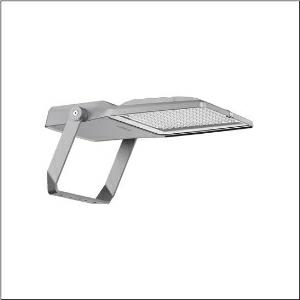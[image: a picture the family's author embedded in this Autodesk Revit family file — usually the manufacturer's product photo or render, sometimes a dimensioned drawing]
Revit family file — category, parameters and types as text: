
# Revit family: floodlight_fl_21_iq_midi___rs12_5xa7782f3b1a_f18b
name_source: partatom
category: Lighting Fixtures
units: mm (PartAtom-declared; Revit-internal decimal feet)

## family parameters
Cut with Voids When Loaded = No
Host = Face
Light Source = No
Part Type = Normal
Room Calculation Point = No
Round Connector Dimension = Use Diameter
Shared = No

## types (1)
- --- (1 x LED, 30610 lm, 270.2 W, 3000K)
    Apparent Load = 270 VA
    CIE Flux Codes = 79 92 99 100 100
    Color Rendering = 80
    Color Temperature = 3000K
    Default Elevation = 1800 mm
    Description = Floodlight FL 21 iQ midi, floodlight, primary light control with lens, of PMMA, primary optical cover: protective disc, of toughened safety glass, transparent, light distribution: RS12, light emission: direct distribution, installation type: surface-mounted, LED, High Power LED, rated luminous flux: 30.610lm, luminous efficacy: 113lm/W, light colour: 830, colour temperature: 3000K, control gear: iQ Street-Remote/DALI, control: optimised constant luminous flux control (CLO 2.0), Desk-Remote (wireless, voltage-free reading and setting of iQ features in the workshop via application-optimized NFC function/RFID function), Smart-Wire, Night-Set, Temp-Guard, Street-Remote, Auto-Match, with terminal, 6-pole, mains connection: 220..240V, AC, 50/60Hz, start of lifetime: 270W, end of service life: 287W, reduction: 117W, luminaire housing, of diecast aluminium, powder-coated, Siteco® metallic grey (DB 702S), corrosivity category C5 mid according to DIN EN ISO 12944, suitable for swimming pools, chlorine-resistant, sealing non-destructively replaceable, mounting bracket, of steel, galvanised, powder-coated, Siteco® metallic grey (DB 702S), protection rating (complete): IP66, insulation class (complete): insulation class II (safety insulation), certification: CE, ENEC, VDE, protection symbol: D, impact resistance: IK08, permissible operating ambient temperature: -40..+40°C, permissible operating ambient temperature for outdoor applications: -40..+50°C, standard: DIN EN 12944, LABS conformity tested according to VDMA 24364:2018-05, packaging unit: 1 piece

Light Distribution: RS12
    Height = 76 mm
    Lamp = 1 x LED
    Lamp Light Flux = 30610 lm
    Lamp Power = 270.2 W
    Lamp count = 1
    Length = 657 mm
    Luminous efficacy = 113 lm/W
    Manufacturer = Siteco
    ModVariant = No
    Model = 5XA7782F3B1A
    Number of Poles = 1
    OnlyDefault = Yes
    Power Factor = 1
    Product Name = Floodlight FL 21 iQ midi | RS12
    Product group = floodlight | pylon annexe
    ProductGroupID = 6200
    Protection Class = Protection class II
    Protection Degree = IP 66
    RLX_Detail_Level = 1
    RLX_Emergency_Light_Flux = 0 lm
    RLX_Emergency_Type = 0
    RLX_Emergency_Type_DB = No
    RlxData = <blob elided: 141257 chars, md5=6ab15098>
    Socket = socket
    Standby Power = 0 W
    System Light Flux = 30610 lm
    System Power = 270 W
    Type Comments = factory setting: luminous flux: 100 % | dim-lin: 254 | 620 mA
    Type Image = l_1006876.jpg
    URL = http://relux.com
    VarID = @adj_107476
    Voltage = 0 V
    Weight = 0.00 kg
    Width = 442 mm

## geometry (parser evidence)
native form markers: Blend x4, Sweep x13
no freeform markers — native parametric forms only
